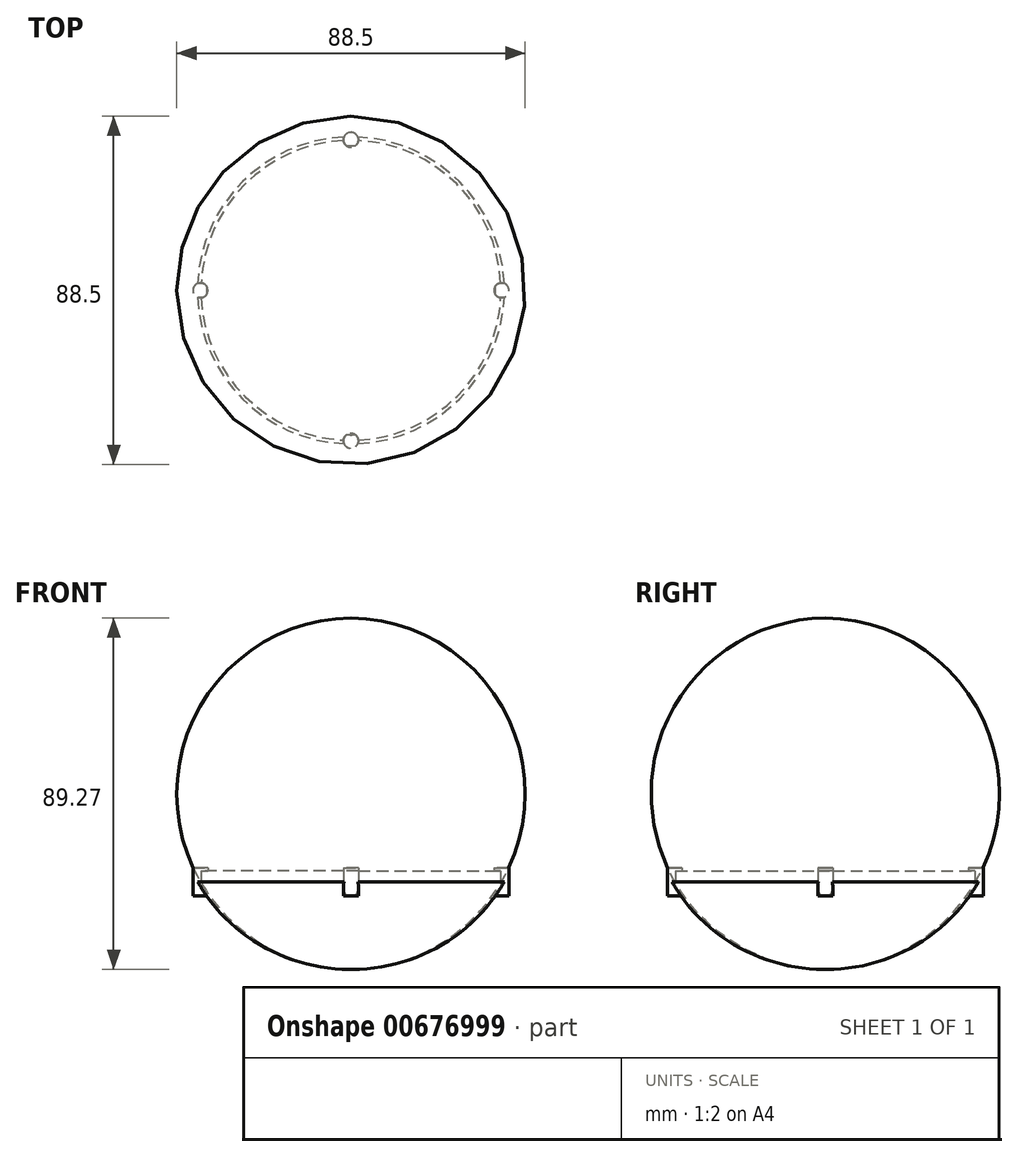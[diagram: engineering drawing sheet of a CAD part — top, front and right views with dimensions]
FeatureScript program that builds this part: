
annotation { "Feature Type Name" : "Feature", "Feature Type Description" : "" }
export const myFeature = defineFeature(function(context is Context, id is Id, definition is map)
    precondition{}
    {
        {
            var Q0;
            Q0=qCreatedBy(makeId("Top.planeOp"),FACE);
            var sketch = newSketch(context, id + "F0", { "sketchPlane" : qUnion([Q0])});
            skCircle(sketch, "E0", {"center": v(0, 0) * mm, "radius": 38.1 * mm});
            skLineSegment(sketch, "E1", {"start": v(-38.1, 0) * mm, "end": v(38.1, 0) * mm});
            skSolve(sketch);
        }
        {
            var Q0;
            Q0=qCreatedBy(makeId("Front.planeOp"),FACE);
            var sketch = newSketch(context, id + "F1", { "sketchPlane" : qUnion([Q0])});
            skArc(sketch, "E2", {"start": v(-38.22, 0) * mm, "mid": v(0.39, -22.24) * mm, "end": v(39, 0) * mm});
            skLineSegment(sketch, "E3", {"start": v(0, 0) * mm, "end": v(0, -22.24) * mm});
            skLineSegment(sketch, "E4", {"start": v(-38.22, 0) * mm, "end": v(39, 0) * mm});
            skSolve(sketch);
        }
        {
            var Q0;
            {var subQ3=sQuery(id+"F1.wireOp",EDGE,"E3");Q0=makeQuery(id+"F1.imprint","IMPRINT",FACE,{"disambiguationData":[TD([[makeQuery(id+"F1.imprint","IMPRINT",EDGE,{"derivedFrom":subQ3}),1.0]])]});}
            var Q1;
            Q1=sQuery(id+"F1.wireOp",EDGE,"E3");
            revolve(context, id + "F2", {"entities" : qUnion([Q0]), "axis" : qUnion([Q1]), "revolveType" : RevolveType.FULL});
        }
        {
            var Q0;
            Q0 = qSketchRegion(id + "F0", true);
            extrude(context, id + "F3", {"entities" : qUnion([Q0]), "operationType" : NewBodyOperationType.ADD, "depth" : 2.8 * mm, "offsetDistance" : 25.4 * mm});
        }
        {
            var Q0;
            Q0=qCreatedBy(makeId("Top.planeOp"),FACE);
            var sketch = newSketch(context, id + "F4", { "sketchPlane" : qUnion([Q0])});
            skCircle(sketch, "E5", {"center": v(0, -38.24) * mm, "radius": 1.9 * mm});
            skCircle(sketch, "E6.1.0", {"center": v(-38.24, 0) * mm, "radius": 1.9 * mm});
            skCircle(sketch, "E6.2.0", {"center": v(0, 38.24) * mm, "radius": 1.9 * mm});
            skCircle(sketch, "E6.3.0", {"center": v(38.24, 0) * mm, "radius": 1.9 * mm});
            skPoint(sketch, "E6.center", {"position": v(0, 0) * mm});
            skLineSegment(sketch, "E6.anchor1", {"start": v(0, 0) * mm, "end": v(0, -38.24) * mm, "construction": true});
            skLineSegment(sketch, "E6.anchor2", {"start": v(0, 0) * mm, "end": v(38.24, 0) * mm, "construction": true});
            skSolve(sketch);
        }
        {
            var Q0;
            Q0=makeQuery(id+"F4.imprint","IMPRINT",FACE,{"disambiguationData":[TD([[makeQuery(id+"F4.imprint","IMPRINT",EDGE,{"derivedFrom":sQuery(id+"F4.wireOp",EDGE,"E6.1.0")}),1.0]])]});
            var Q1;
            Q1=makeQuery(id+"F4.imprint","IMPRINT",FACE,{"disambiguationData":[TD([[makeQuery(id+"F4.imprint","IMPRINT",EDGE,{"derivedFrom":sQuery(id+"F4.wireOp",EDGE,"E5")}),1.0]])]});
            var Q2;
            Q2=makeQuery(id+"F4.imprint","IMPRINT",FACE,{"disambiguationData":[TD([[makeQuery(id+"F4.imprint","IMPRINT",EDGE,{"derivedFrom":sQuery(id+"F4.wireOp",EDGE,"E6.3.0")}),1.0]])]});
            var Q3;
            Q3=makeQuery(id+"F4.imprint","IMPRINT",FACE,{"disambiguationData":[TD([[makeQuery(id+"F4.imprint","IMPRINT",EDGE,{"derivedFrom":sQuery(id+"F4.wireOp",EDGE,"E6.2.0")}),1.0]])]});
            var Q4;
            Q4=sQuery(id+"F4.wireOp",EDGE,"E6.1.0");
            var Q5;
            Q5=sQuery(id+"F4.wireOp",EDGE,"E5");
            var Q6;
            Q6=sQuery(id+"F4.wireOp",EDGE,"E6.3.0");
            var Q7;
            Q7=sQuery(id+"F4.wireOp",EDGE,"E6.2.0");
            extrude(context, id + "F5", {"entities" : qUnion([Q0, Q1, Q2, Q3]), "operationType" : NewBodyOperationType.ADD, "surfaceEntities" : qUnion([Q4, Q5, Q6, Q7]), "endBound" : BoundingType.SYMMETRIC, "depth" : 7.11 * mm, "offsetDistance" : 25.4 * mm});
        }
    });
